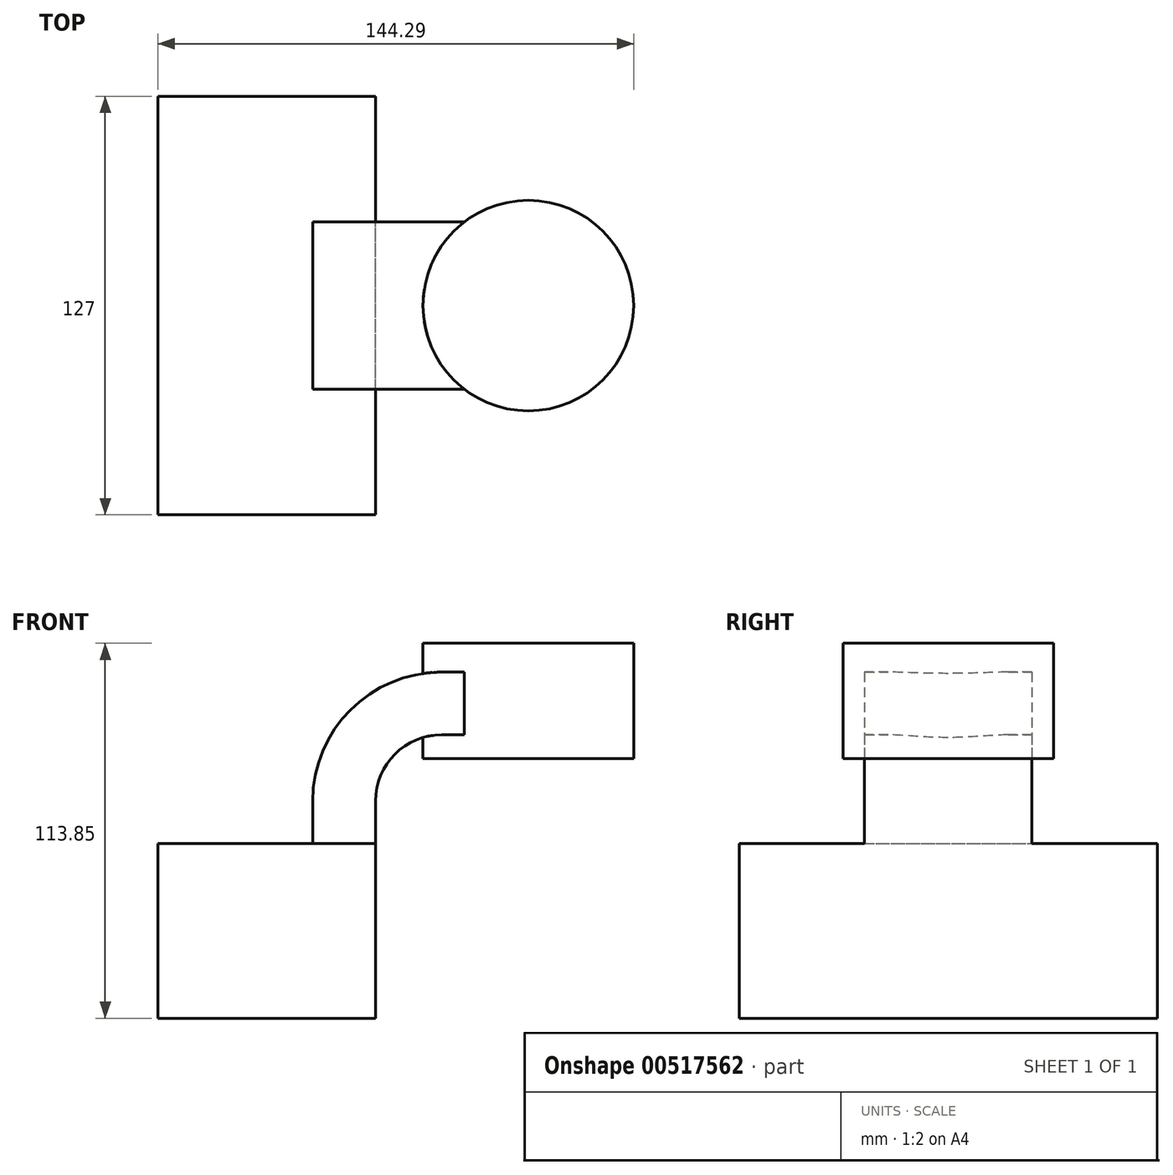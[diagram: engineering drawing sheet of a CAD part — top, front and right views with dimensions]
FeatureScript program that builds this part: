
annotation { "Feature Type Name" : "Feature", "Feature Type Description" : "" }
export const myFeature = defineFeature(function(context is Context, id is Id, definition is map)
    precondition{}
    {
        {
            var Q0;
            Q0=qCreatedBy(makeId("Front.planeOp"),FACE);
            var sketch = newSketch(context, id + "F0", { "sketchPlane" : qUnion([Q0])});
            skLineSegment(sketch, "E0.bottom", {"start": v(32.98, 26.5) * mm, "end": v(-32.98, 26.5) * mm});
            skLineSegment(sketch, "E0.top", {"start": v(32.98, -26.5) * mm, "end": v(-32.98, -26.5) * mm});
            skLineSegment(sketch, "E0.left", {"start": v(32.98, 26.5) * mm, "end": v(32.98, -26.5) * mm});
            skLineSegment(sketch, "E0.right", {"start": v(-32.98, 26.5) * mm, "end": v(-32.98, -26.5) * mm});
            skPoint(sketch, "E0.middle", {"position": v(0, 0) * mm});
            skLineSegment(sketch, "E1.bottom", {"start": v(111.31, 87.35) * mm, "end": v(68.02, 87.35) * mm});
            skLineSegment(sketch, "E1.top", {"start": v(111.31, 52.3) * mm, "end": v(68.02, 52.3) * mm});
            skLineSegment(sketch, "E1.left", {"start": v(111.31, 87.35) * mm, "end": v(111.31, 52.3) * mm});
            skLineSegment(sketch, "E1.right", {"start": v(68.02, 87.35) * mm, "end": v(68.02, 52.3) * mm});
            skPoint(sketch, "E1.middle", {"position": v(89.67, 69.83) * mm});
            skLineSegment(sketch, "E2", {"start": v(32.98, 26.5) * mm, "end": v(32.98, 39.42) * mm});
            skArc(sketch, "E3", {"start": v(32.98, 39.42) * mm, "mid": v(38.87, 53.63) * mm, "end": v(53.08, 59.52) * mm});
            skLineSegment(sketch, "E4", {"start": v(53.08, 59.52) * mm, "end": v(79.36, 59.52) * mm});
            skLineSegment(sketch, "E5.0", {"start": v(53.08, 78.57) * mm, "end": v(79.36, 78.57) * mm});
            skArc(sketch, "E5.1", {"start": v(13.93, 39.42) * mm, "mid": v(25.4, 67.1) * mm, "end": v(53.08, 78.57) * mm});
            skLineSegment(sketch, "E5.2", {"start": v(13.93, 26.5) * mm, "end": v(13.93, 39.42) * mm});
            skLineSegment(sketch, "E6", {"start": v(79.36, 59.52) * mm, "end": v(79.36, 87.35) * mm});
            skLineSegment(sketch, "E7", {"start": v(79.36, 59.52) * mm, "end": v(79.36, 52.3) * mm});
            skSolve(sketch);
        }
        {
            var Q0;
            Q0=makeQuery(id+"F0.imprint","IMPRINT",FACE,{"disambiguationData":[TD([[makeQuery(id+"F0.imprint","IMPRINT",EDGE,{"derivedFrom":sQuery(id+"F0.wireOp",EDGE,"E0.top")}),-1.0]])]});
            extrude(context, id + "F1", {"entities" : qUnion([Q0]), "endBound" : BoundingType.SYMMETRIC, "depth" : 127 * mm});
        }
        {
            var Q0;
            {var subQ1=sQuery(id+"F0.wireOp",EDGE,"E2");Q0=makeQuery(id+"F0.imprint","IMPRINT",FACE,{"disambiguationData":[TD([[makeQuery(id+"F0.imprint","IMPRINT",EDGE,{"derivedFrom":subQ1}),1.0]])]});}
            var Q1;
            {var subQ0=sQuery(id+"F0.wireOp",EDGE,"E5.0");var subQ1=sQuery(id+"F0.wireOp",EDGE,"E1.right");var subQ2=makeQuery(id+"F0.imprint","INTERSECT",VERTEX,{"derivedFrom":[subQ1,subQ0]});Q1=makeQuery(id+"F0.imprint","IMPRINT",FACE,{"disambiguationData":[TD([[makeQuery(id+"F0.imprint","IMPRINT",EDGE,{"disambiguationData":[TD([[subQ2,-1.0]])],"derivedFrom":subQ1}),1.0]])]});}
            extrude(context, id + "F2", {"entities" : qUnion([Q0, Q1]), "operationType" : NewBodyOperationType.ADD, "endBound" : BoundingType.SYMMETRIC, "depth" : 50.8 * mm});
        }
        {
            var Q0;
            {var subQ3=sQuery(id+"F0.wireOp",EDGE,"E1.left");Q0=makeQuery(id+"F0.imprint","IMPRINT",FACE,{"disambiguationData":[TD([[makeQuery(id+"F0.imprint","IMPRINT",EDGE,{"derivedFrom":subQ3}),-1.0]])]});}
            var Q1;
            Q1=sQuery(id+"F0.wireOp",EDGE,"E6");
            revolve(context, id + "F3", {"operationType" : NewBodyOperationType.ADD, "entities" : qUnion([Q0]), "axis" : qUnion([Q1]), "revolveType" : RevolveType.FULL});
        }
    });
